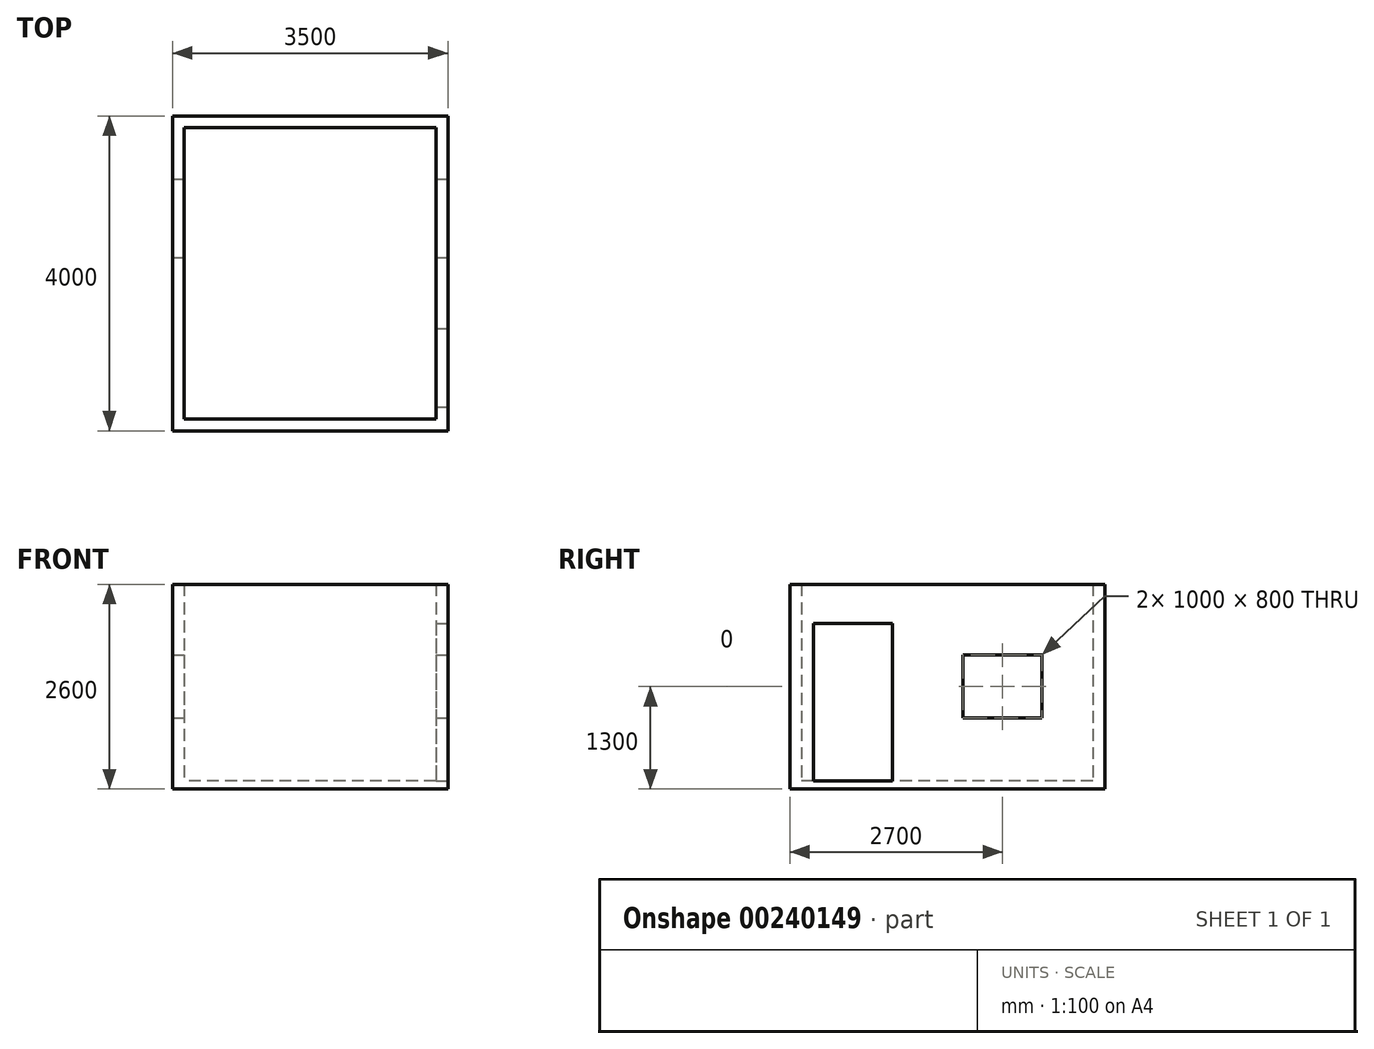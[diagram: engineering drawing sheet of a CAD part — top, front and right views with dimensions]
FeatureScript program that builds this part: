
annotation { "Feature Type Name" : "Feature", "Feature Type Description" : "" }
export const myFeature = defineFeature(function(context is Context, id is Id, definition is map)
    precondition{}
    {
        {
            var Q0;
            Q0=qCreatedBy(makeId("Top.planeOp"),FACE);
            var sketch = newSketch(context, id + "F0", { "sketchPlane" : qUnion([Q0])});
            skLineSegment(sketch, "E0.bottom", {"start": v(1750, 2000) * mm, "end": v(-1750, 2000) * mm});
            skLineSegment(sketch, "E0.top", {"start": v(1750, -2000) * mm, "end": v(-1750, -2000) * mm});
            skLineSegment(sketch, "E0.left", {"start": v(1750, 2000) * mm, "end": v(1750, -2000) * mm});
            skLineSegment(sketch, "E0.right", {"start": v(-1750, 2000) * mm, "end": v(-1750, -2000) * mm});
            skPoint(sketch, "E0.middle", {"position": v(0, 0) * mm});
            skLineSegment(sketch, "E1.0", {"start": v(1600, 1850) * mm, "end": v(-1600, 1850) * mm});
            skLineSegment(sketch, "E1.1", {"start": v(1600, 1850) * mm, "end": v(1600, -1850) * mm});
            skLineSegment(sketch, "E1.2", {"start": v(1600, -1850) * mm, "end": v(-1600, -1850) * mm});
            skLineSegment(sketch, "E1.3", {"start": v(-1600, 1850) * mm, "end": v(-1600, -1850) * mm});
            skSolve(sketch);
        }
        {
            var Q0;
            Q0=makeQuery(id+"F0.imprint","IMPRINT",FACE,{"disambiguationData":[TD([[makeQuery(id+"F0.imprint","IMPRINT",EDGE,{"derivedFrom":sQuery(id+"F0.wireOp",EDGE,"E0.bottom")}),1.0]])]});
            extrude(context, id + "F1", {"entities" : qUnion([Q0]), "depth" : 2500 * mm});
        }
        {
            var Q0;
            Q0=makeQuery(id+"F1.opExtrude","SWEPT_FACE",FACE,{"disambiguationData":[OSD([sQuery(id+"F0.wireOp",EDGE,"E0.left")])]});
            var sketch = newSketch(context, id + "F2", { "sketchPlane" : qUnion([Q0])});
            skLineSegment(sketch, "E2", {"start": v(-2000, 0) * mm, "end": v(-1700, 0) * mm});
            skLineSegment(sketch, "E3.bottom", {"start": v(-1700, 0) * mm, "end": v(-700, 0) * mm});
            skLineSegment(sketch, "E3.top", {"start": v(-1700, 2000) * mm, "end": v(-700, 2000) * mm});
            skLineSegment(sketch, "E3.left", {"start": v(-1700, 0) * mm, "end": v(-1700, 2000) * mm});
            skLineSegment(sketch, "E3.right", {"start": v(-700, 0) * mm, "end": v(-700, 2000) * mm});
            skSolve(sketch);
        }
        {
            var Q0;
            Q0=makeQuery(id+"F2.imprint","IMPRINT",FACE,{"disambiguationData":[TD([[makeQuery(id+"F2.imprint","IMPRINT",EDGE,{"derivedFrom":sQuery(id+"F2.wireOp",EDGE,"E3.bottom")}),-1.0]])]});
            extrude(context, id + "F3", {"entities" : qUnion([Q0]), "operationType" : NewBodyOperationType.REMOVE, "endBound" : BoundingType.UP_TO_NEXT, "oppositeDirection" : true, "depth" : 25 * mm});
        }
        {
            var Q0;
            Q0=makeQuery(id+"F1.opExtrude","SWEPT_FACE",FACE,{"disambiguationData":[OSD([sQuery(id+"F0.wireOp",EDGE,"E0.left")])]});
            var sketch = newSketch(context, id + "F4", { "sketchPlane" : qUnion([Q0])});
            skLineSegment(sketch, "E4", {"start": v(2000, 0) * mm, "end": v(1200, 0) * mm});
            skLineSegment(sketch, "E5", {"start": v(1200, 0) * mm, "end": v(1200, 800) * mm});
            skLineSegment(sketch, "E6", {"start": v(1200, 800) * mm, "end": v(200, 800) * mm});
            skLineSegment(sketch, "E7", {"start": v(200, 800) * mm, "end": v(200, 1600) * mm});
            skLineSegment(sketch, "E8", {"start": v(200, 1600) * mm, "end": v(1200, 1600) * mm});
            skLineSegment(sketch, "E9", {"start": v(1200, 1600) * mm, "end": v(1200, 800) * mm});
            skSolve(sketch);
        }
        {
            var Q0;
            Q0 = qSketchRegion(id + "F4", true);
            extrude(context, id + "F5", {"entities" : qUnion([Q0]), "operationType" : NewBodyOperationType.REMOVE, "endBound" : BoundingType.THROUGH_ALL, "oppositeDirection" : true, "depth" : 25 * mm});
        }
        {
            var Q0;
            Q0=makeQuery(id+"F1.opExtrude","CAP_FACE",FACE,{"disambiguationData":[OSD([sQuery(id+"F0.wireOp",EDGE,"E0.bottom"),sQuery(id+"F0.wireOp",EDGE,"E0.top"),sQuery(id+"F0.wireOp",EDGE,"E0.left"),sQuery(id+"F0.wireOp",EDGE,"E0.right"),sQuery(id+"F0.wireOp",EDGE,"E1.0"),sQuery(id+"F0.wireOp",EDGE,"E1.1"),sQuery(id+"F0.wireOp",EDGE,"E1.2"),sQuery(id+"F0.wireOp",EDGE,"E1.3")])],"isStart":true});
            var sketch = newSketch(context, id + "F6", { "sketchPlane" : qUnion([Q0])});
            skLineSegment(sketch, "E10.bottom", {"start": v(-1750, 2000) * mm, "end": v(1750, 2000) * mm});
            skLineSegment(sketch, "E10.top", {"start": v(-1750, -2000) * mm, "end": v(1750, -2000) * mm});
            skLineSegment(sketch, "E10.left", {"start": v(-1750, 2000) * mm, "end": v(-1750, -2000) * mm});
            skLineSegment(sketch, "E10.right", {"start": v(1750, 2000) * mm, "end": v(1750, -2000) * mm});
            skSolve(sketch);
        }
        {
            var Q0;
            Q0 = qSketchRegion(id + "F6", true);
            extrude(context, id + "F7", {"entities" : qUnion([Q0]), "operationType" : NewBodyOperationType.ADD, "depth" : 100 * mm});
        }
    });
